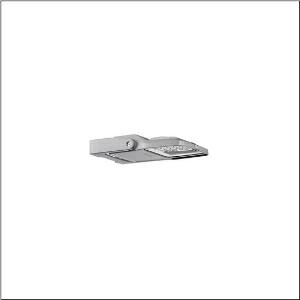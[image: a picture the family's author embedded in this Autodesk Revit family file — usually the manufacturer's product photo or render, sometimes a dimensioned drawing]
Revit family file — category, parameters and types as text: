
# Revit family: floodlight_fl_21_iq_micro___pl61_5xa7761a4c2a_08ca
name_source: partatom
category: Lighting Fixtures
units: mm (PartAtom-declared; Revit-internal decimal feet)

## family parameters
Cut with Voids When Loaded = No
Host = Face
Light Source = No
Part Type = Normal
Room Calculation Point = No
Round Connector Dimension = Use Diameter
Shared = No

## types (1)
- --- (1 x LED, 3030 lm, 23.1 W, 4000K)
    Apparent Load = 23 VA
    CIE Flux Codes = 33 65 98 100 100
    Color Rendering = 70
    Color Temperature = 4000K
    Default Elevation = 1800 mm
    Description = Floodlight FL 21 iQ micro, floodlight, primary light control with lens, of PMMA, primary optical cover: protective disc, of toughened safety glass, transparent, light distribution: PL61, light emission: direct distribution, installation type: surface-mounted, LED, High Power LED, rated luminous flux: 3.030lm, luminous efficacy: 131lm/W, light colour: 740, colour temperature: 4000K, control: optimised constant luminous flux control (CLO 2.0), Desk-Remote (wireless, voltage-free reading and setting of iQ features in the workshop via application-optimized NFC function/RFID function), Light-Fading, Smart-Wire, Night-Set, Lumen-Switch, Temp-Guard, Auto-Match, with terminal, 6-pole, mains connection: 220..240V, AC, 50/60Hz, start of lifetime: 23W, end of service life: 24W, reduction: 11W, luminaire housing, of diecast aluminium, powder-coated, Siteco® metallic grey (DB 702S), corrosivity category C5 mid according to DIN EN ISO 12944, sealing non-destructively replaceable, design bracket, of diecast aluminium, powder-coated, Siteco® metallic grey (DB 702S), protection rating (complete): IP66, insulation class (complete): insulation class II (safety insulation), certification: CE, ENEC, VDE, protection symbol: D, impact resistance: IK07, permissible operating ambient temperature: -40..+40°C, permissible operating ambient temperature for outdoor applications: -40..+50°C, standard: DIN EN 12944, LABS conformity tested according to VDMA 24364:2018-05, packaging unit: 1 piece

Light Distribution: PL61
    Height = 65 mm
    Lamp = 1 x LED
    Lamp Light Flux = 3030 lm
    Lamp Power = 23.1 W
    Lamp count = 1
    Length = 312 mm
    Luminous efficacy = 131 lm/W
    Manufacturer = Siteco
    ModVariant = No
    Model = 5XA7761A4C2A
    Mounting Place = Wall
    Mounting Type = Surface mounted
    Number of Poles = 1
    OnlyDefault = Yes
    Power Factor = 1
    Product Name = Floodlight FL 21 iQ micro | PL61
    Product group = floodlight | wall mounted
    ProductGroupID = 2001
    Protection Class = Protection class II
    Protection Degree = IP 66
    RLX_Detail_Level = 1
    RLX_Emergency_Light_Flux = 0 lm
    RLX_Emergency_Type = 0
    RLX_Emergency_Type_DB = No
    RlxData = <blob elided: 97597 chars, md5=f6eeb876>
    Socket = socket
    Standby Power = 0 W
    System Light Flux = 3030 lm
    System Power = 23 W
    Type Comments = factory setting: luminous flux: 100 % | dim-lin: 254 | 455 mA
    Type Image = l_1006878.jpg
    URL = http://relux.com
    VarID = @adj_129055
    Voltage = 0 V
    Weight = 0.00 kg
    Width = 230 mm

## geometry (parser evidence)
native form markers: Blend x4, Sweep x12
no freeform markers — native parametric forms only
